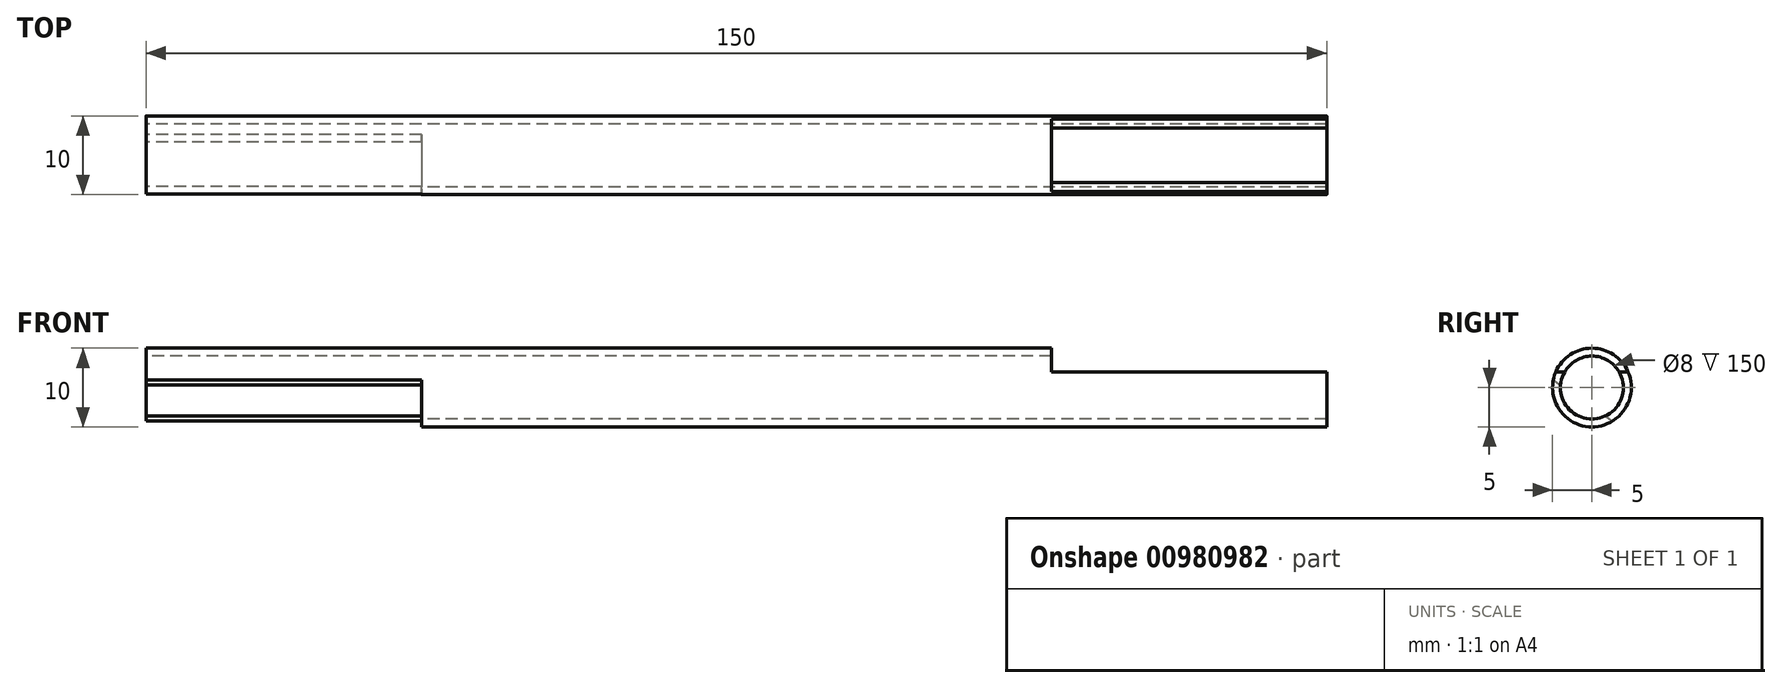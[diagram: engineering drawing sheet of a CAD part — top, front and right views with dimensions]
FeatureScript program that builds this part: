
annotation { "Feature Type Name" : "Feature", "Feature Type Description" : "" }
export const myFeature = defineFeature(function(context is Context, id is Id, definition is map)
    precondition{}
    {
        {
            var Q0;
            Q0=qCreatedBy(makeId("Right.planeOp"),FACE);
            var sketch = newSketch(context, id + "F0", { "sketchPlane" : qUnion([Q0])});
            skCircle(sketch, "E0", {"center": v(0, 0) * mm, "radius": 4 * mm});
            skCircle(sketch, "E1", {"center": v(0, 0) * mm, "radius": 5 * mm});
            skSolve(sketch);
        }
        {
            var Q0;
            Q0=makeQuery(id+"F0.imprint","IMPRINT",FACE,{"disambiguationData":[TD([[makeQuery(id+"F0.imprint","IMPRINT",EDGE,{"derivedFrom":sQuery(id+"F0.wireOp",EDGE,"E0")}),-1.0]])]});
            extrude(context, id + "F1", {"entities" : qUnion([Q0]), "depth" : 150 * mm, "offsetDistance" : 25 * mm});
        }
        {
            var Q0;
            Q0=qCreatedBy(makeId("Front.planeOp"),FACE);
            var sketch = newSketch(context, id + "F2", { "sketchPlane" : qUnion([Q0])});
            skLineSegment(sketch, "E2.bottom", {"start": v(150, 2) * mm, "end": v(115, 2) * mm});
            skLineSegment(sketch, "E2.top", {"start": v(150, 12) * mm, "end": v(115, 12) * mm});
            skLineSegment(sketch, "E2.left", {"start": v(150, 2) * mm, "end": v(150, 12) * mm});
            skLineSegment(sketch, "E2.right", {"start": v(115, 2) * mm, "end": v(115, 12) * mm});
            skLineSegment(sketch, "E3.bottom", {"start": v(0, 12) * mm, "end": v(35, 12) * mm});
            skLineSegment(sketch, "E3.top", {"start": v(0, 2) * mm, "end": v(35, 2) * mm});
            skLineSegment(sketch, "E3.left", {"start": v(0, 12) * mm, "end": v(0, 2) * mm});
            skLineSegment(sketch, "E3.right", {"start": v(35, 12) * mm, "end": v(35, 2) * mm});
            skLineSegment(sketch, "E4.0", {"start": v(150, 5) * mm, "end": v(150, -5) * mm});
            skLineSegment(sketch, "E5", {"start": v(0, 0) * mm, "end": v(202.22, 0) * mm, "construction": true});
            skSolve(sketch);
        }
        {
            var Q0;
            {var subQ1=sQuery(id+"F2.wireOp",EDGE,"E2.bottom");Q0=makeQuery(id+"F2.imprint","IMPRINT",FACE,{"disambiguationData":[TD([[makeQuery(id+"F2.imprint","IMPRINT",EDGE,{"derivedFrom":subQ1}),-1.0]])]});}
            extrude(context, id + "F3", {"entities" : qUnion([Q0]), "operationType" : NewBodyOperationType.REMOVE, "endBound" : BoundingType.SYMMETRIC, "oppositeDirection" : true, "depth" : 10 * mm, "offsetDistance" : 25 * mm});
        }
        {
            var Q0;
            Q0=sQuery(id+"F2.wireOp",EDGE,"E5");
            cPlane(context, id + "F4", {"entities" : qUnion([Q0]), "cplaneType" : CPlaneType.LINE_ANGLE, "offset" : 25 * mm, "angle" : 214.73 * degree, "oppositeDirection" : true, "width" : 150 * mm, "height" : 150 * mm});
        }
        {
            var Q0;
            Q0=qCreatedBy(id+"F4.planeOp",FACE);
            var sketch = newSketch(context, id + "F5", { "sketchPlane" : qUnion([Q0])});
            skLineSegment(sketch, "E6", {"start": v(-186.22, -5.6) * mm, "end": v(16, -5.6) * mm, "construction": true});
            skLineSegment(sketch, "E7.bottom", {"start": v(0, -12) * mm, "end": v(35, -12) * mm});
            skLineSegment(sketch, "E7.top", {"start": v(0, -2) * mm, "end": v(35, -2) * mm});
            skLineSegment(sketch, "E7.left", {"start": v(0, -12) * mm, "end": v(0, -2) * mm});
            skLineSegment(sketch, "E7.right", {"start": v(35, -12) * mm, "end": v(35, -2) * mm});
            skSolve(sketch);
        }
        {
            var Q0;
            Q0=makeQuery(id+"F5.imprint","IMPRINT",FACE,{"disambiguationData":[TD([[makeQuery(id+"F5.imprint","IMPRINT",EDGE,{"derivedFrom":sQuery(id+"F5.wireOp",EDGE,"E7.bottom")}),1.0]])]});
            extrude(context, id + "F6", {"entities" : qUnion([Q0]), "operationType" : NewBodyOperationType.REMOVE, "endBound" : BoundingType.SYMMETRIC, "depth" : 25 * mm, "offsetDistance" : 25 * mm});
        }
    });
